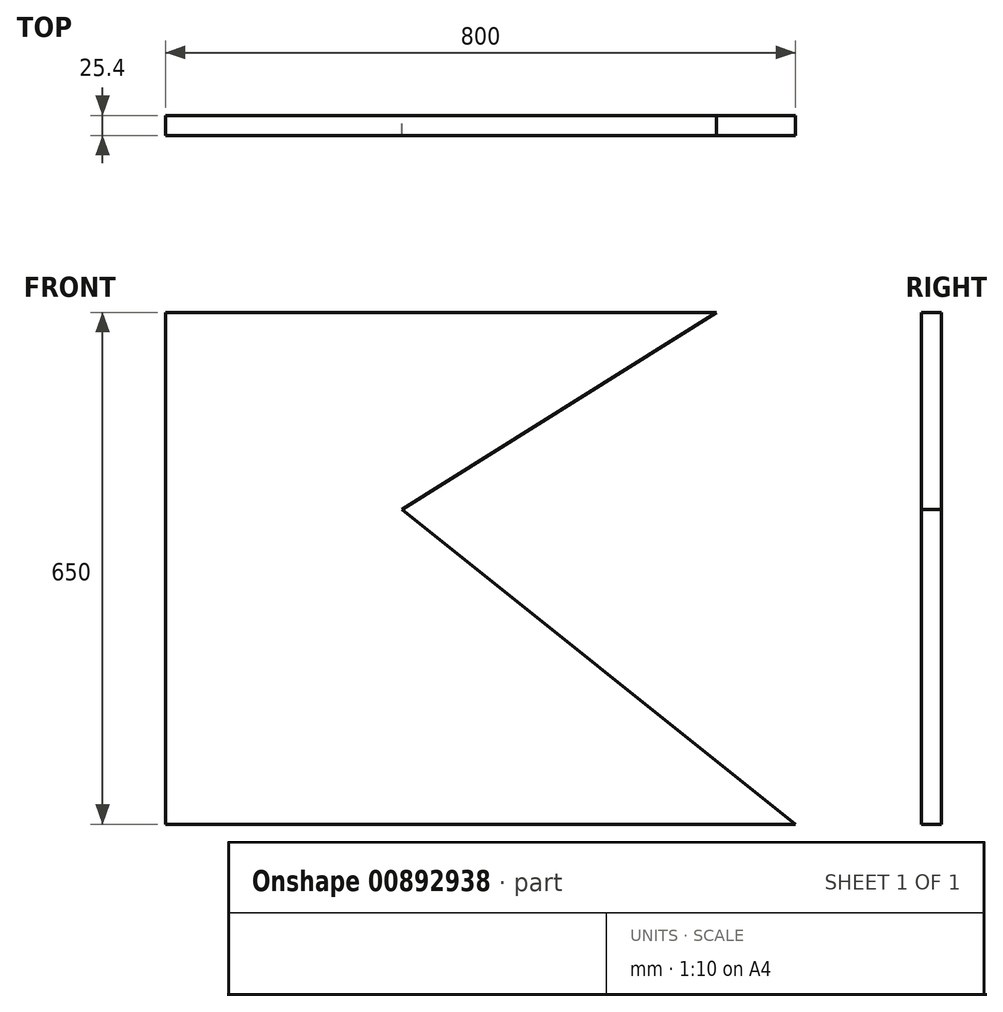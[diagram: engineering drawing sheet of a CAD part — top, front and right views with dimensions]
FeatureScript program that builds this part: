
annotation { "Feature Type Name" : "Feature", "Feature Type Description" : "" }
export const myFeature = defineFeature(function(context is Context, id is Id, definition is map)
    precondition{}
    {
        {
            var Q0;
            Q0=qCreatedBy(makeId("Front.planeOp"),FACE);
            var sketch = newSketch(context, id + "F0", { "sketchPlane" : qUnion([Q0])});
            skLineSegment(sketch, "E0", {"start": v(700, 650) * mm, "end": v(0, 650) * mm});
            skLineSegment(sketch, "E1", {"start": v(0, 0) * mm, "end": v(800, 0) * mm});
            skLineSegment(sketch, "E2", {"start": v(700, 650) * mm, "end": v(300, 400) * mm});
            skLineSegment(sketch, "E3", {"start": v(300, 400) * mm, "end": v(800, 0) * mm});
            skLineSegment(sketch, "E4", {"start": v(0, 650) * mm, "end": v(0, 0) * mm});
            skSolve(sketch);
        }
        {
            var Q0;
            Q0=makeQuery(id+"F0.imprint","IMPRINT",FACE,{"disambiguationData":[TD([[makeQuery(id+"F0.imprint","IMPRINT",EDGE,{"derivedFrom":sQuery(id+"F0.wireOp",EDGE,"E0")}),1.0]])]});
            extrude(context, id + "F1", {"entities" : qUnion([Q0]), "depth" : 25.4 * mm, "offsetDistance" : 25.4 * mm});
        }
    });
